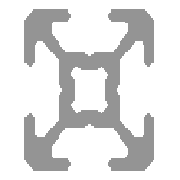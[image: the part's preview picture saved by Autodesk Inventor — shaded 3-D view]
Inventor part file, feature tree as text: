
AUTODESK INVENTOR PART (.ipt)
format: ipt  version: 2015 (Build 190159000, 159)  size: 376,832 bytes
history: native  units: mm
features: other x3, extrude x1, sketch x1
ambient origin geometry x8: Origin, YZ Plane, XZ Plane, XY Plane, X Axis, Y Axis, Z Axis, Center Point
bodies: Body1 (feature_tree)
feature tree (5):
  other  "Blocks"
  extrude  "Extrusion3"  [1 undecoded]
  sketch  "Sketch1"  dims[d23=0.0mm]
  other  "20x20"
  other  "20x20:1"
note: 1 required parameter value undecoded (feature->parameter linkage not recoverable at this tier; creation-order binding heuristic only, values carry confidence <= 0.55)
